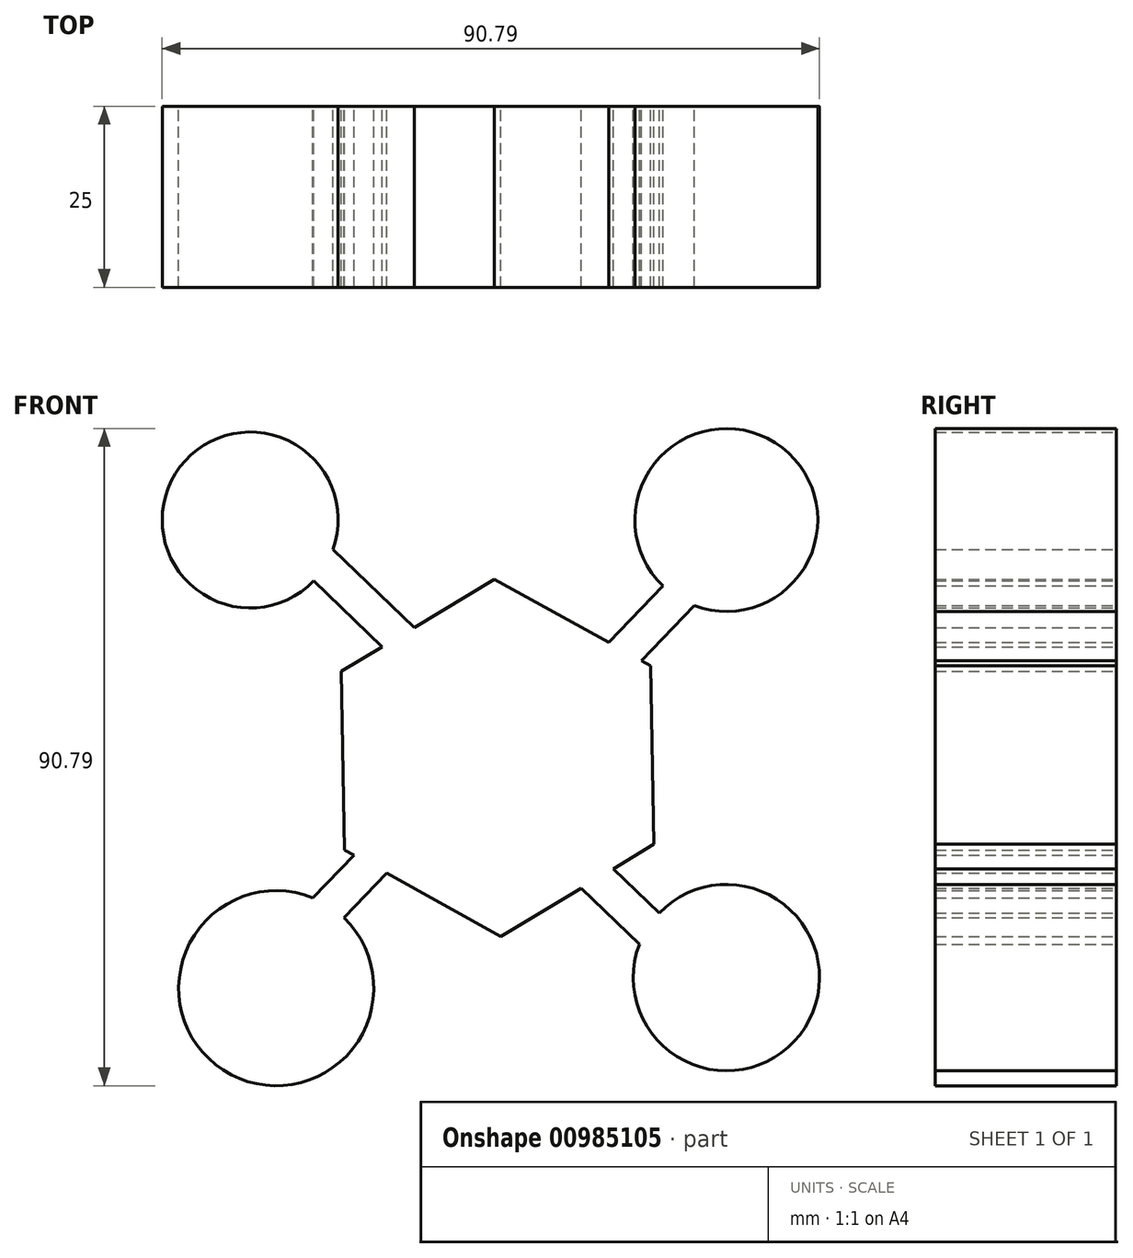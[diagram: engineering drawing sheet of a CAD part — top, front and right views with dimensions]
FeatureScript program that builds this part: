
annotation { "Feature Type Name" : "Feature", "Feature Type Description" : "" }
export const myFeature = defineFeature(function(context is Context, id is Id, definition is map)
    precondition{}
    {
        {
            var Q0;
            Q0=qCreatedBy(makeId("Front.planeOp"),FACE);
            var sketch = newSketch(context, id + "F0", { "sketchPlane" : qUnion([Q0])});
            skLineSegment(sketch, "E0", {"start": v(0, -2.4) * mm, "end": v(31.58, 30.45) * mm});
            skLineSegment(sketch, "E1", {"start": v(0, -2.4) * mm, "end": v(-34.19, 30.45) * mm});
            skLineSegment(sketch, "E2", {"start": v(0, -2.4) * mm, "end": v(31.58, -32.77) * mm});
            skLineSegment(sketch, "E3", {"start": v(0, -2.4) * mm, "end": v(-30.58, -34.23) * mm});
            skCircle(sketch, "E4", {"center": v(31.58, 30.45) * mm, "radius": 12.63 * mm});
            skCircle(sketch, "E5", {"center": v(-34.19, 30.45) * mm, "radius": 12.15 * mm});
            skCircle(sketch, "E6", {"center": v(31.58, -32.77) * mm, "radius": 12.87 * mm});
            skCircle(sketch, "E7", {"center": v(-30.58, -34.23) * mm, "radius": 13.48 * mm});
            skCircle(sketch, "E8.cCircle", {"center": v(0, -2.4) * mm, "radius": 21.36 * mm, "construction": true});
            skLineSegment(sketch, "E8.0", {"start": v(-0.45, 22.26) * mm, "end": v(21.13, 10.32) * mm});
            skLineSegment(sketch, "E8.1", {"start": v(21.13, 10.32) * mm, "end": v(21.59, -14.35) * mm});
            skLineSegment(sketch, "E8.2", {"start": v(21.59, -14.35) * mm, "end": v(0.45, -27.07) * mm});
            skLineSegment(sketch, "E8.3", {"start": v(0.45, -27.07) * mm, "end": v(-21.13, -15.13) * mm});
            skLineSegment(sketch, "E8.4", {"start": v(-21.13, -15.13) * mm, "end": v(-21.59, 9.53) * mm});
            skLineSegment(sketch, "E8.5", {"start": v(-21.59, 9.53) * mm, "end": v(-0.45, 22.26) * mm});
            skPoint(sketch, "E8.0.midPoint", {"position": v(10.34, 16.29) * mm});
            skLineSegment(sketch, "E9", {"start": v(-30.58, -34.23) * mm, "end": v(-24.51, -40.06) * mm});
            skLineSegment(sketch, "E10", {"start": v(-30.58, -34.23) * mm, "end": v(-36.95, -28.1) * mm});
            skLineSegment(sketch, "E11", {"start": v(31.58, -32.77) * mm, "end": v(26.09, -38.49) * mm});
            skLineSegment(sketch, "E12", {"start": v(31.58, -32.77) * mm, "end": v(37, -27.13) * mm});
            skLineSegment(sketch, "E13", {"start": v(31.58, 30.45) * mm, "end": v(38.38, 27.62) * mm});
            skLineSegment(sketch, "E14", {"start": v(31.58, 30.45) * mm, "end": v(28.1, 33.8) * mm});
            skLineSegment(sketch, "E15", {"start": v(-34.19, 30.45) * mm, "end": v(-26.49, 33.8) * mm});
            skLineSegment(sketch, "E16.0", {"start": v(3.46, 1.2) * mm, "end": v(-30.72, 34.06) * mm});
            skLineSegment(sketch, "E17.0", {"start": v(3.6, -5.87) * mm, "end": v(35.19, 26.99) * mm});
            skLineSegment(sketch, "E18.0", {"start": v(-3.46, -6.01) * mm, "end": v(28.12, -36.37) * mm});
            skLineSegment(sketch, "E19.0", {"start": v(-3.6, 1.06) * mm, "end": v(-34.19, -30.76) * mm});
            skSolve(sketch);
        }
        {
            var Q0;
            Q0 = qSketchRegion(id + "F0", true);
            extrude(context, id + "F1", {"entities" : qUnion([Q0]), "depth" : 25 * mm, "offsetDistance" : 25 * mm});
        }
    });
